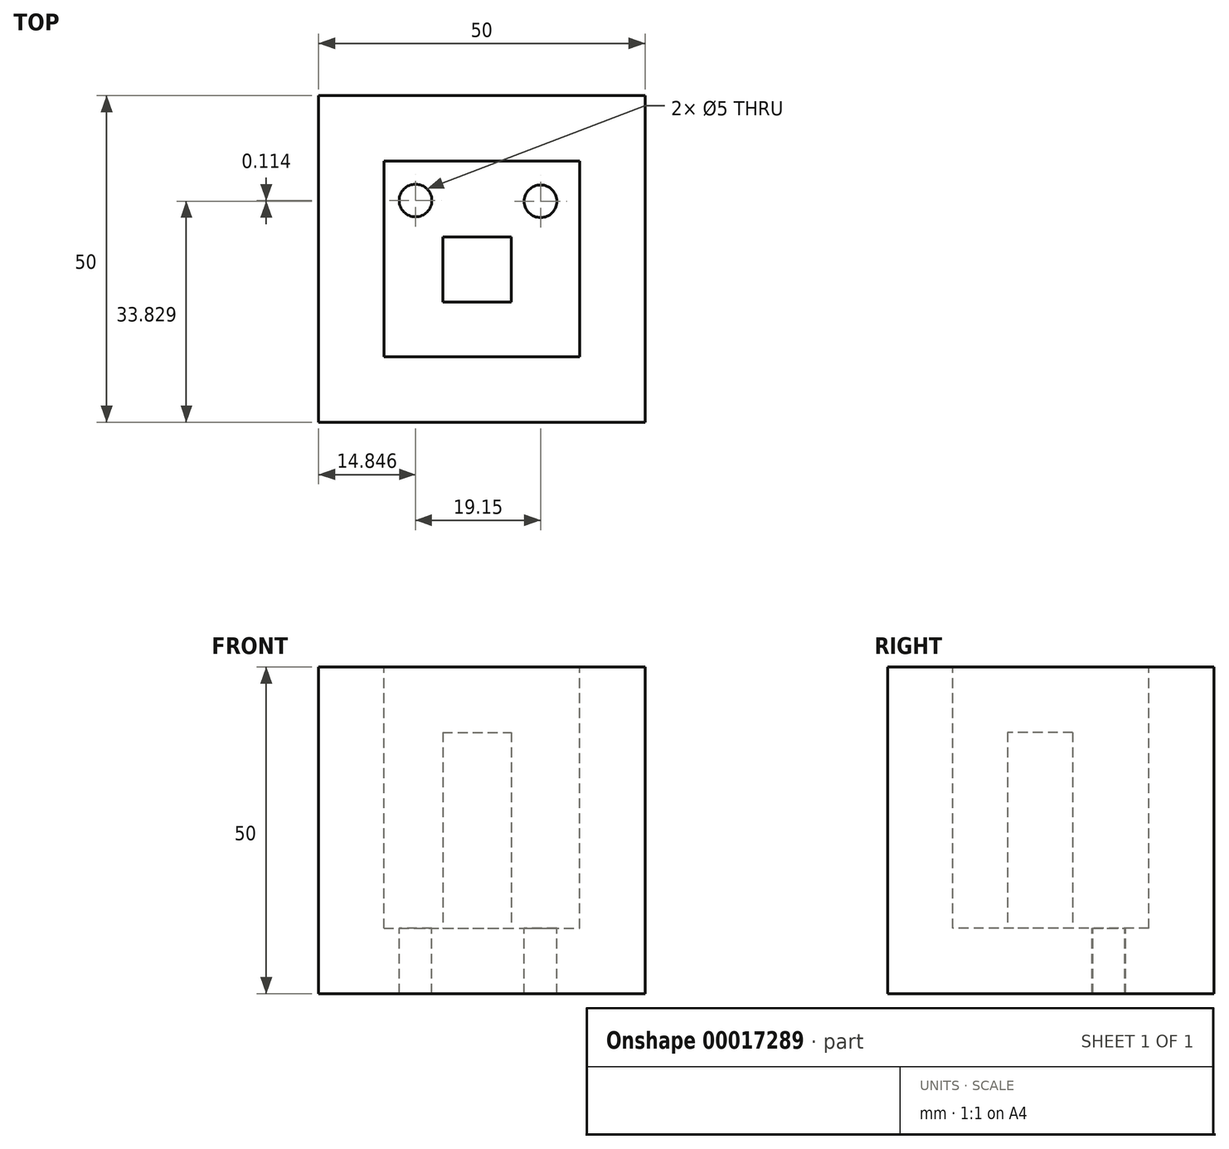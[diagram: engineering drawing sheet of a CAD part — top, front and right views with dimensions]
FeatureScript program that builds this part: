
annotation { "Feature Type Name" : "Feature", "Feature Type Description" : "" }
export const myFeature = defineFeature(function(context is Context, id is Id, definition is map)
    precondition{}
    {
        {
            var Q0;
            Q0=qCreatedBy(makeId("Front.planeOp"),FACE);
            var sketch = newSketch(context, id + "F0", { "sketchPlane" : qUnion([Q0])});
            skLineSegment(sketch, "E0.bottom", {"start": v(-86.68, 0) * mm, "end": v(-36.68, 0) * mm});
            skLineSegment(sketch, "E0.top", {"start": v(-86.68, -50) * mm, "end": v(-36.68, -50) * mm});
            skLineSegment(sketch, "E0.left", {"start": v(-86.68, 0) * mm, "end": v(-86.68, -50) * mm});
            skLineSegment(sketch, "E0.right", {"start": v(-36.68, 0) * mm, "end": v(-36.68, -50) * mm});
            skSolve(sketch);
        }
        {
            var Q0;
            Q0 = qSketchRegion(id + "F0", true);
            extrude(context, id + "F1", {"entities" : qUnion([Q0]), "oppositeDirection" : true, "depth" : 50 * mm});
        }
        {
            var Q0;
            Q0=makeQuery(id+"F1.opExtrude","CAP_FACE",FACE,{"disambiguationData":[OSD([sQuery(id+"F0.wireOp",EDGE,"E0.bottom"),sQuery(id+"F0.wireOp",EDGE,"E0.top"),sQuery(id+"F0.wireOp",EDGE,"E0.left"),sQuery(id+"F0.wireOp",EDGE,"E0.right")])],"isStart":true});
            shell(context, id + "F2", {"entities" : qUnion([Q0]), "thickness" : 10 * mm});
        }
        {
            var Q0;
            Q0=makeQuery(id+"F2.opShell","OFFSET_FACE",FACE,{"disambiguationData":[OSD([sQuery(id+"F0.wireOp",EDGE,"E0.bottom"),sQuery(id+"F0.wireOp",EDGE,"E0.top"),sQuery(id+"F0.wireOp",EDGE,"E0.left"),sQuery(id+"F0.wireOp",EDGE,"E0.right")])]});
            var sketch = newSketch(context, id + "F3", { "sketchPlane" : qUnion([Q0])});
            skLineSegment(sketch, "E1.bottom", {"start": v(-67.66, -21.64) * mm, "end": v(-57.15, -21.64) * mm});
            skLineSegment(sketch, "E1.top", {"start": v(-67.66, -31.6) * mm, "end": v(-57.15, -31.6) * mm});
            skLineSegment(sketch, "E1.left", {"start": v(-67.66, -21.64) * mm, "end": v(-67.66, -31.6) * mm});
            skLineSegment(sketch, "E1.right", {"start": v(-57.15, -21.64) * mm, "end": v(-57.15, -31.6) * mm});
            skSolve(sketch);
        }
        {
            var Q0;
            Q0=makeQuery(id+"F3.imprint","IMPRINT",FACE,{"disambiguationData":[TD([[makeQuery(id+"F3.imprint","IMPRINT",EDGE,{"derivedFrom":sQuery(id+"F3.wireOp",EDGE,"E1.bottom")}),-1.0]])]});
            extrude(context, id + "F4", {"entities" : qUnion([Q0]), "operationType" : NewBodyOperationType.ADD, "depth" : 30 * mm});
        }
        {
            var Q0;
            Q0=makeQuery(id+"F2.opShell","OFFSET_FACE",FACE,{"disambiguationData":[OSD([sQuery(id+"F0.wireOp",EDGE,"E0.bottom"),sQuery(id+"F0.wireOp",EDGE,"E0.top"),sQuery(id+"F0.wireOp",EDGE,"E0.left"),sQuery(id+"F0.wireOp",EDGE,"E0.right")])]});
            var sketch = newSketch(context, id + "F5", { "sketchPlane" : qUnion([Q0])});
            skPoint(sketch, "E2", {"position": v(-71.83, -16.06) * mm});
            skPoint(sketch, "E3", {"position": v(-52.37, -16.06) * mm});
            skPoint(sketch, "E4", {"position": v(-52.37, -11.53) * mm});
            skLineSegment(sketch, "E5", {"start": v(-71.83, -16.06) * mm, "end": v(-52.37, -16.06) * mm});
            skSolve(sketch);
        }
        {
            var Q0;
            Q0=sQuery(id+"F5.wireOp",VERTEX,"E2");
            var Q1;
            Q1=makeQuery(id+"F1.opExtrude","SWEPT_BODY",BODY,{"disambiguationData":[OSD([sQuery(id+"F0.wireOp",EDGE,"E0.bottom"),sQuery(id+"F0.wireOp",EDGE,"E0.top"),sQuery(id+"F0.wireOp",EDGE,"E0.left"),sQuery(id+"F0.wireOp",EDGE,"E0.right")])]});
            hole(context, id + "F6", {"style" : HoleStyle.SIMPLE, "holeDiameter" : 5 * mm, "endStyle" : HoleEndStyle.THROUGH, "locations" : qUnion([Q0]), "scope" : qUnion([Q1])});
        }
        {
            var Q0;
            Q0=makeQuery(id+"F2.opShell","OFFSET_FACE",FACE,{"disambiguationData":[OSD([sQuery(id+"F0.wireOp",EDGE,"E0.bottom"),sQuery(id+"F0.wireOp",EDGE,"E0.top"),sQuery(id+"F0.wireOp",EDGE,"E0.left"),sQuery(id+"F0.wireOp",EDGE,"E0.right")])]});
            var sketch = newSketch(context, id + "F7", { "sketchPlane" : qUnion([Q0])});
            skPoint(sketch, "E6", {"position": v(-52.68, -15.6) * mm});
            skPoint(sketch, "E7", {"position": v(-52.68, -16.17) * mm});
            skSolve(sketch);
        }
        {
            var Q0;
            Q0=sQuery(id+"F7.wireOp",VERTEX,"E7");
            var Q1;
            Q1=makeQuery(id+"F1.opExtrude","SWEPT_BODY",BODY,{"disambiguationData":[OSD([sQuery(id+"F0.wireOp",EDGE,"E0.bottom"),sQuery(id+"F0.wireOp",EDGE,"E0.top"),sQuery(id+"F0.wireOp",EDGE,"E0.left"),sQuery(id+"F0.wireOp",EDGE,"E0.right")])]});
            hole(context, id + "F8", {"style" : HoleStyle.SIMPLE, "holeDiameter" : 5 * mm, "endStyle" : HoleEndStyle.THROUGH, "locations" : qUnion([Q0]), "scope" : qUnion([Q1])});
        }
        {
            var Q0;
            Q0=makeQuery(id+"F1.opExtrude","SWEPT_BODY",BODY,{"disambiguationData":[OSD([sQuery(id+"F0.wireOp",EDGE,"E0.bottom"),sQuery(id+"F0.wireOp",EDGE,"E0.top"),sQuery(id+"F0.wireOp",EDGE,"E0.left"),sQuery(id+"F0.wireOp",EDGE,"E0.right")])]});
            var Q1;
            Q1=makeQuery(id+"F1.opExtrude","CAP_EDGE",EDGE,{"disambiguationData":[OSD([sQuery(id+"F0.wireOp",EDGE,"E0.top")])],"isStart":false});
            transform(context, id + "F9", {"entities" : qUnion([Q0]), "transformType" : TransformType.ROTATION, "transformAxis" : qUnion([Q1]), "angle" : 90 * degree, "oppositeDirection" : true, "makeCopy" : false});
        }
    });
